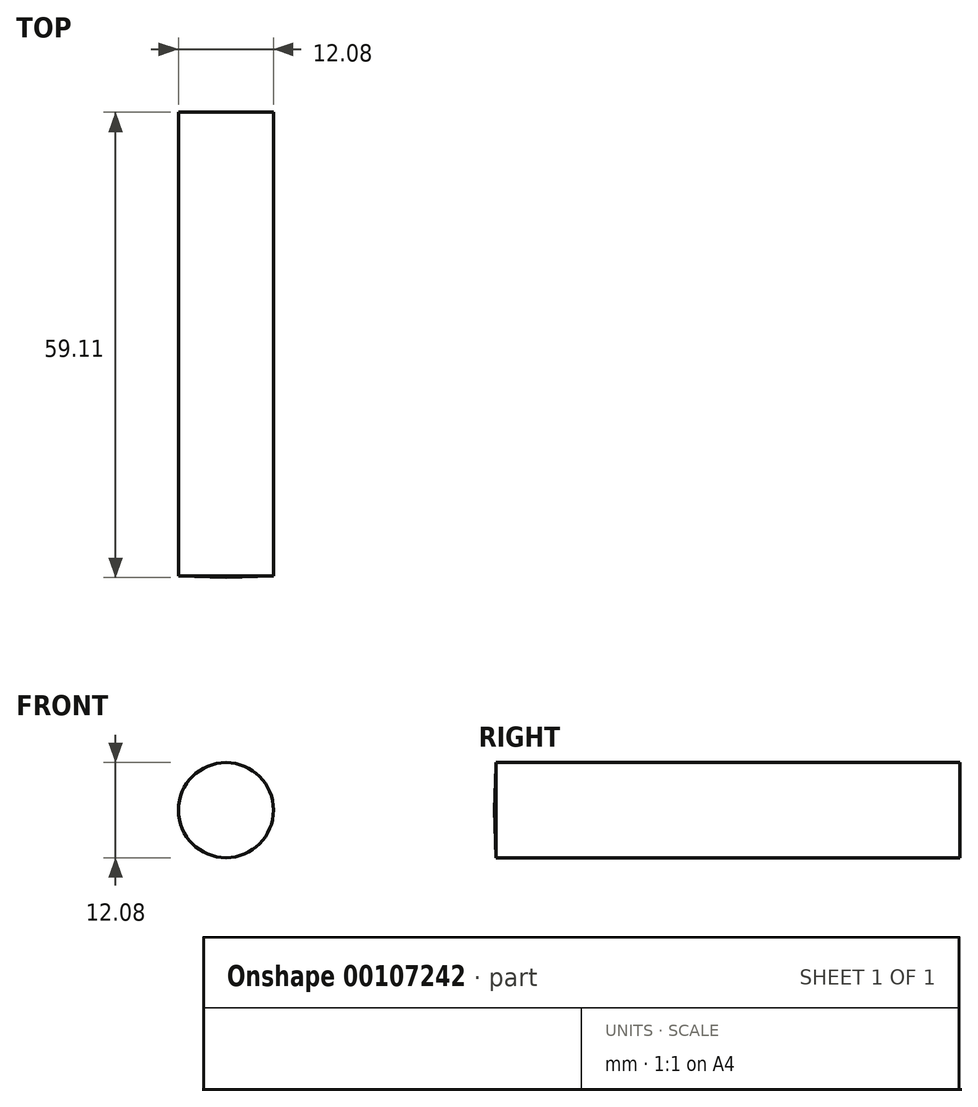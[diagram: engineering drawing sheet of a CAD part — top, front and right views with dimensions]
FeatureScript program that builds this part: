
annotation { "Feature Type Name" : "Feature", "Feature Type Description" : "" }
export const myFeature = defineFeature(function(context is Context, id is Id, definition is map)
    precondition{}
    {
        {
            var Q0;
            Q0=qCreatedBy(makeId("Right.planeOp"),FACE);
            var sketch = newSketch(context, id + "F0", { "sketchPlane" : qUnion([Q0])});
            skLineSegment(sketch, "E0", {"start": v(-30.43, 0) * mm, "end": v(28.68, 0) * mm});
            skLineSegment(sketch, "E1", {"start": v(28.68, 0) * mm, "end": v(28.68, 6.04) * mm});
            skLineSegment(sketch, "E2", {"start": v(28.68, 6.04) * mm, "end": v(-30.22, 6.04) * mm});
            skLineSegment(sketch, "E3", {"start": v(-30.22, 6.04) * mm, "end": v(-30.43, 0) * mm});
            skSolve(sketch);
        }
        {
            var Q0;
            Q0 = qSketchRegion(id + "F0", true);
            var Q1;
            Q1=sQuery(id+"F0.wireOp",EDGE,"E0");
            revolve(context, id + "F1", {"entities" : qUnion([Q0]), "axis" : qUnion([Q1]), "revolveType" : RevolveType.FULL});
        }
    });
